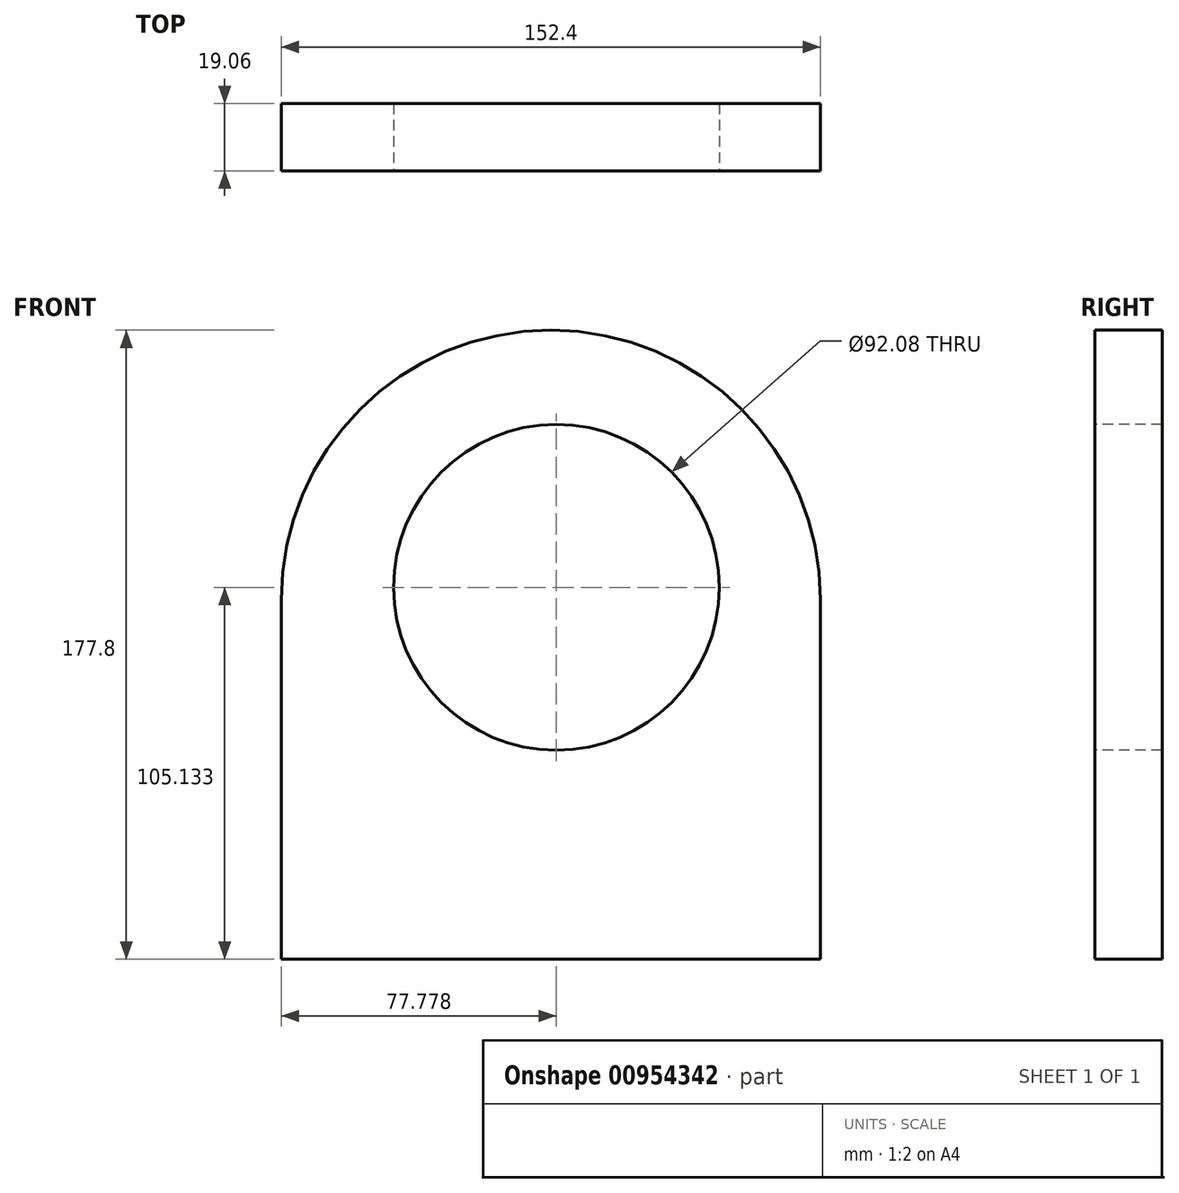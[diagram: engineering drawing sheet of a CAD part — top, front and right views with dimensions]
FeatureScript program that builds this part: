
annotation { "Feature Type Name" : "Feature", "Feature Type Description" : "" }
export const myFeature = defineFeature(function(context is Context, id is Id, definition is map)
    precondition{}
    {
        {
            var Q0;
            Q0=qCreatedBy(makeId("Front.planeOp"),FACE);
            var sketch = newSketch(context, id + "F0", { "sketchPlane" : qUnion([Q0])});
            skLineSegment(sketch, "E0.bottom", {"start": v(32.22, 0) * mm, "end": v(-120.18, 0) * mm});
            skLineSegment(sketch, "E0.top", {"start": v(32.22, 101.6) * mm, "end": v(-120.18, 101.6) * mm});
            skLineSegment(sketch, "E0.left", {"start": v(32.22, 0) * mm, "end": v(32.22, 101.6) * mm});
            skLineSegment(sketch, "E0.right", {"start": v(-120.18, 0) * mm, "end": v(-120.18, 101.6) * mm});
            skPoint(sketch, "E0.middle", {"position": v(-43.98, 50.8) * mm});
            skArc(sketch, "E1", {"start": v(32.22, 101.6) * mm, "mid": v(-43.98, 177.8) * mm, "end": v(-120.18, 101.6) * mm});
            skSolve(sketch);
        }
        {
            var Q0;
            Q0=makeQuery(id+"F0.imprint","IMPRINT",FACE,{"disambiguationData":[TD([[makeQuery(id+"F0.imprint","IMPRINT",EDGE,{"derivedFrom":sQuery(id+"F0.wireOp",EDGE,"E0.bottom")}),-1.0]])]});
            cPlane(context, id + "F1", {"entities" : qUnion([Q0]), "cplaneType" : CPlaneType.OFFSET, "offset" : 25.4 * mm, "width" : 152.4 * mm, "height" : 152.4 * mm});
        }
        {
            var Q0;
            Q0=makeQuery(id+"F0.imprint","IMPRINT",FACE,{"disambiguationData":[TD([[makeQuery(id+"F0.imprint","IMPRINT",EDGE,{"derivedFrom":sQuery(id+"F0.wireOp",EDGE,"E0.bottom")}),-1.0]])]});
            var Q1;
            Q1=makeQuery(id+"F0.imprint","IMPRINT",FACE,{"disambiguationData":[TD([[makeQuery(id+"F0.imprint","IMPRINT",EDGE,{"derivedFrom":sQuery(id+"F0.wireOp",EDGE,"E0.top")}),-1.0]])]});
            extrude(context, id + "F2", {"entities" : qUnion([Q0, Q1]), "depth" : 19.05 * mm, "offsetDistance" : 25.4 * mm, "symmetric" : true});
        }
        {
            var Q0;
            Q0=qCreatedBy(id+"F1.planeOp",FACE);
            var sketch = newSketch(context, id + "F3", { "sketchPlane" : qUnion([Q0])});
            skPoint(sketch, "E2", {"position": v(-42.4, 105.13) * mm});
            skSolve(sketch);
        }
        {
            var Q0;
            Q0=sQuery(id+"F3.wireOp",VERTEX,"E2");
            var Q1;
            Q1=makeQuery(id+"F2.opExtrude","SWEPT_BODY",BODY,{"disambiguationData":[OSD([sQuery(id+"F0.wireOp",EDGE,"E0.bottom"),sQuery(id+"F0.wireOp",EDGE,"E0.left"),sQuery(id+"F0.wireOp",EDGE,"E0.right"),sQuery(id+"F0.wireOp",EDGE,"E1")])]});
            hole(context, id + "F4", {"style" : HoleStyle.SIMPLE, "endStyle" : HoleEndStyle.THROUGH, "holeDiameter" : 92.07 * mm, "majorDiameter" : 6.35 * mm, "isTappedThrough" : true, "tappedDepth" : 12.7 * mm, "tapClearance" : 3, "locations" : qUnion([Q0]), "scope" : qUnion([Q1])});
        }
    });
